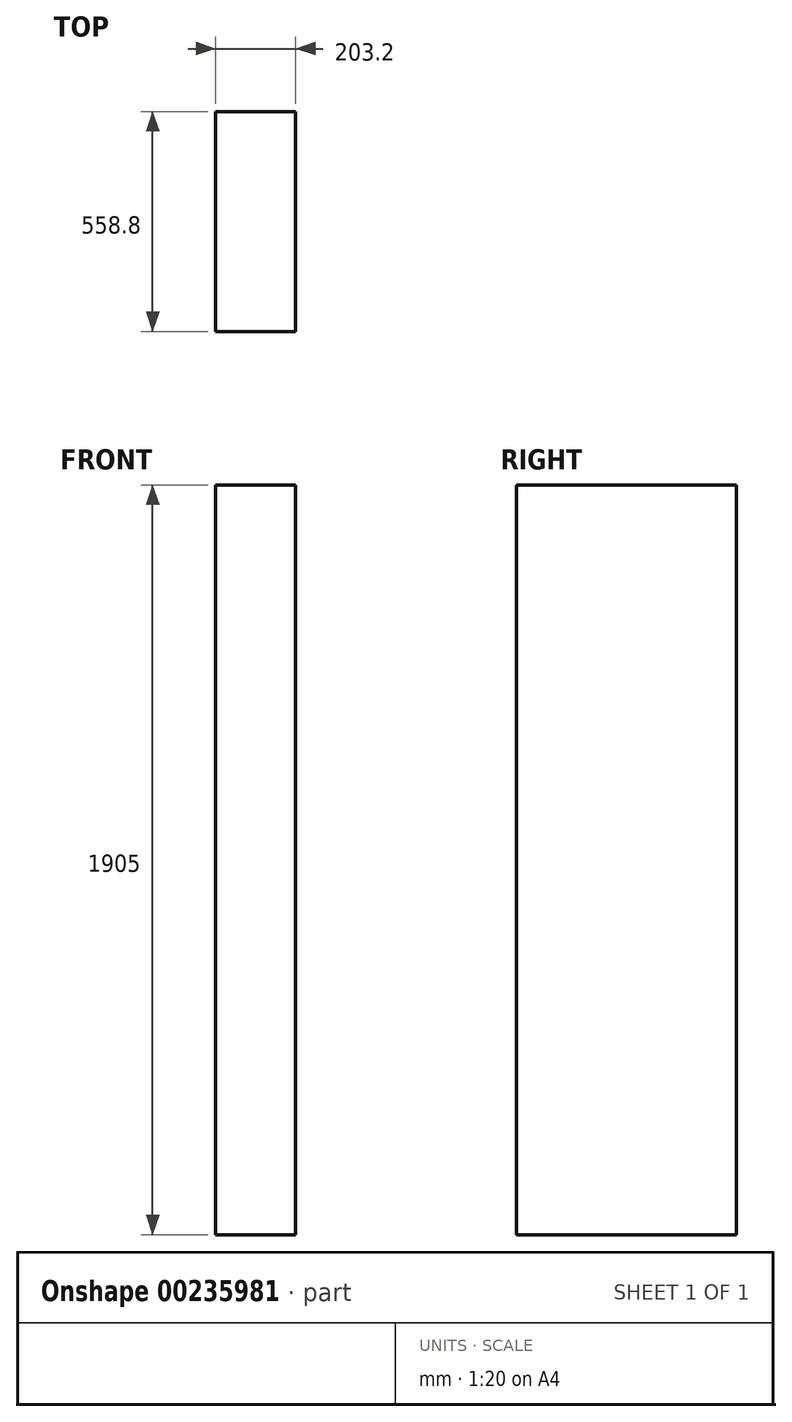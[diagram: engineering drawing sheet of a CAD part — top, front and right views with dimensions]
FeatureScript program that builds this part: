
annotation { "Feature Type Name" : "Feature", "Feature Type Description" : "" }
export const myFeature = defineFeature(function(context is Context, id is Id, definition is map)
    precondition{}
    {
        {
            var Q0;
            Q0=qCreatedBy(makeId("Top.planeOp"),FACE);
            var sketch = newSketch(context, id + "F0", { "sketchPlane" : qUnion([Q0])});
            skLineSegment(sketch, "E0.bottom", {"start": v(101.6, -279.4) * mm, "end": v(-101.6, -279.4) * mm});
            skLineSegment(sketch, "E0.top", {"start": v(101.6, 279.4) * mm, "end": v(-101.6, 279.4) * mm});
            skLineSegment(sketch, "E0.left", {"start": v(101.6, -279.4) * mm, "end": v(101.6, 279.4) * mm});
            skLineSegment(sketch, "E0.right", {"start": v(-101.6, -279.4) * mm, "end": v(-101.6, 279.4) * mm});
            skPoint(sketch, "E0.middle", {"position": v(0, 0) * mm});
            skSolve(sketch);
        }
        {
            var Q0;
            Q0 = qSketchRegion(id + "F0", true);
            extrude(context, id + "F1", {"entities" : qUnion([Q0]), "depth" : 1905 * mm});
        }
        {
            var Q0;
            Q0=makeQuery(id+"F1.opExtrude","CAP_FACE",FACE,{"disambiguationData":[OSD([sQuery(id+"F0.wireOp",EDGE,"E0.bottom"),sQuery(id+"F0.wireOp",EDGE,"E0.top"),sQuery(id+"F0.wireOp",EDGE,"E0.left"),sQuery(id+"F0.wireOp",EDGE,"E0.right")])],"isStart":false});
            var sketch = newSketch(context, id + "F2", { "sketchPlane" : qUnion([Q0])});
            skLineSegment(sketch, "E1.bottom", {"start": v(101.6, 268.92) * mm, "end": v(115.6, 268.92) * mm});
            skLineSegment(sketch, "E1.top", {"start": v(101.6, -268.92) * mm, "end": v(115.6, -268.92) * mm});
            skLineSegment(sketch, "E1.left", {"start": v(101.6, 268.92) * mm, "end": v(101.6, -268.92) * mm});
            skLineSegment(sketch, "E1.right", {"start": v(115.6, 268.92) * mm, "end": v(115.6, -268.92) * mm});
            skSolve(sketch);
        }
        {
            var Q0;
            Q0 = qSketchRegion(id + "F2", true);
            extrude(context, id + "F3", {"entities" : qUnion([Q0]), "depth" : 1905 * mm});
        }
        {
            var Q0;
            Q0=makeQuery(id+"F3.opExtrude","SWEPT_BODY",BODY,{"disambiguationData":[OSD([sQuery(id+"F2.wireOp",EDGE,"E1.bottom"),sQuery(id+"F2.wireOp",EDGE,"E1.top"),sQuery(id+"F2.wireOp",EDGE,"E1.left"),sQuery(id+"F2.wireOp",EDGE,"E1.right")])]});
            deleteBodies(context, id + "F4", {"entities" : qUnion([Q0])});
        }
    });
